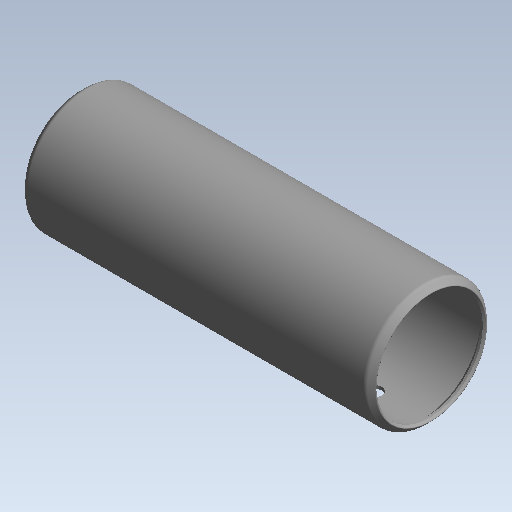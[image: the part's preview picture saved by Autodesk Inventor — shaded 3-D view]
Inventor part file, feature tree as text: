
AUTODESK INVENTOR PART (.ipt)
format: ipt  version: 2020 (Build 240168000, 168)  size: 156,160 bytes
history: native  units: mm (DEFAULTED — no unit token found)
features: other x42, sketch x2, revolve x1, extrude x1
ambient origin geometry x8: Origin, YZ Plane, XZ Plane, XY Plane, X Axis, Y Axis, Z Axis, Center Point
bodies: Solid1 (feature_tree)
feature tree (46):
  revolve  "Revolution1"  [1 undecoded]
  extrude  "Extrusion1"  [1 undecoded]
  other  "cp1_XY"
  other  "cp1_YZ"
  other  "cp1_ZX"
  other  "cp1_X"
  other  "cp1_Y"
  other  "cp1_Z"
  other  "cp1_Center"
  other  "cp2_XY"
  other  "cp2_YZ"
  other  "cp2_ZX"
  other  "cp2_X"
  other  "cp2_Y"
  other  "cp2_Z"
  other  "cp2_Center"
  other  "cp3_XY"
  other  "cp3_YZ"
  other  "cp3_ZX"
  other  "cp3_X"
  other  "cp3_Y"
  other  "cp3_Z"
  other  "cp3_Center"
  other  "cp4_XY"
  other  "cp4_YZ"
  other  "cp4_ZX"
  other  "cp4_X"
  other  "cp4_Y"
  other  "cp4_Z"
  other  "cp4_Center"
  other  "tube_front_XY"
  other  "tube_front_YZ"
  other  "tube_front_ZX"
  other  "tube_front_X"
  other  "tube_front_Y"
  other  "tube_front_Z"
  other  "tube_front_Center"
  other  "tube_rear_XY"
  other  "tube_rear_YZ"
  other  "tube_rear_ZX"
  other  "tube_rear_X"
  other  "tube_rear_Y"
  other  "tube_rear_Z"
  other  "tube_rear_Center"
  sketch  "Sketch_1"  dims[d0=360.0deg d1=10.2235mm d2=0.0mm]
  sketch  "Sketch_4"
note: 2 required parameter values undecoded (feature->parameter linkage not recoverable at this tier; creation-order binding heuristic only, values carry confidence <= 0.55)